# Revit family: Seating-Casual-Naughtone-Busby_Left_Hand1
name_source: partatom
category: Furniture
revit_build: Autodesk Revit 2014 (Build: 20130308_1515(x64)
units: mm (PartAtom-declared; Revit-internal decimal feet)

## types (1)
- BUS-L
    Additional Materials = Additional finish and material options available. Please contact Naughtone direct for further informaton.
    AssetIdentifier = BUS-L
    Barcode = 0
    COBie Description = Designed by Samir Skalli, Busby is a modern day cocoon for everyday situations. Used in a variety of applications Busby works particularly well as a haven for employees in open plan work spaces, suitable for one person to make confidential phone calls, and with the ability to place two or more pieces together for a more collaborative arrangement.
    Cost = 0 $
    Current Revision = 1
    Depth = 650 mm
    Description = Busby Chair
    Height = 1300 mm  [stored 4.26509 ft]
    Length = 850 mm
    Manufacturer = Naughtone
    Model = Busby Chair
    Name = Furniture-Seating-Casual-Busby_Chair
    Option = Left Hand
    Product Code = BUS-L
    Product URL = http://www.naughtone.com
    Seat Height = 430 mm
    SerialNumber = 0
    TagNumber = 0
    TypeName = 850mmx650mmx1300mm Busby Chair
    URL = http://www.naughtone.com
    Uniclass = Pr_40_50_12_57
    WarrantyDuration = 60

note: [stored X ft] marks values corroborated as IEEE doubles in the binary element streams (Revit-internal decimal feet)

## geometry (parser evidence)
native form markers: Blend x6, Sweep x4
no freeform markers — native parametric forms only
